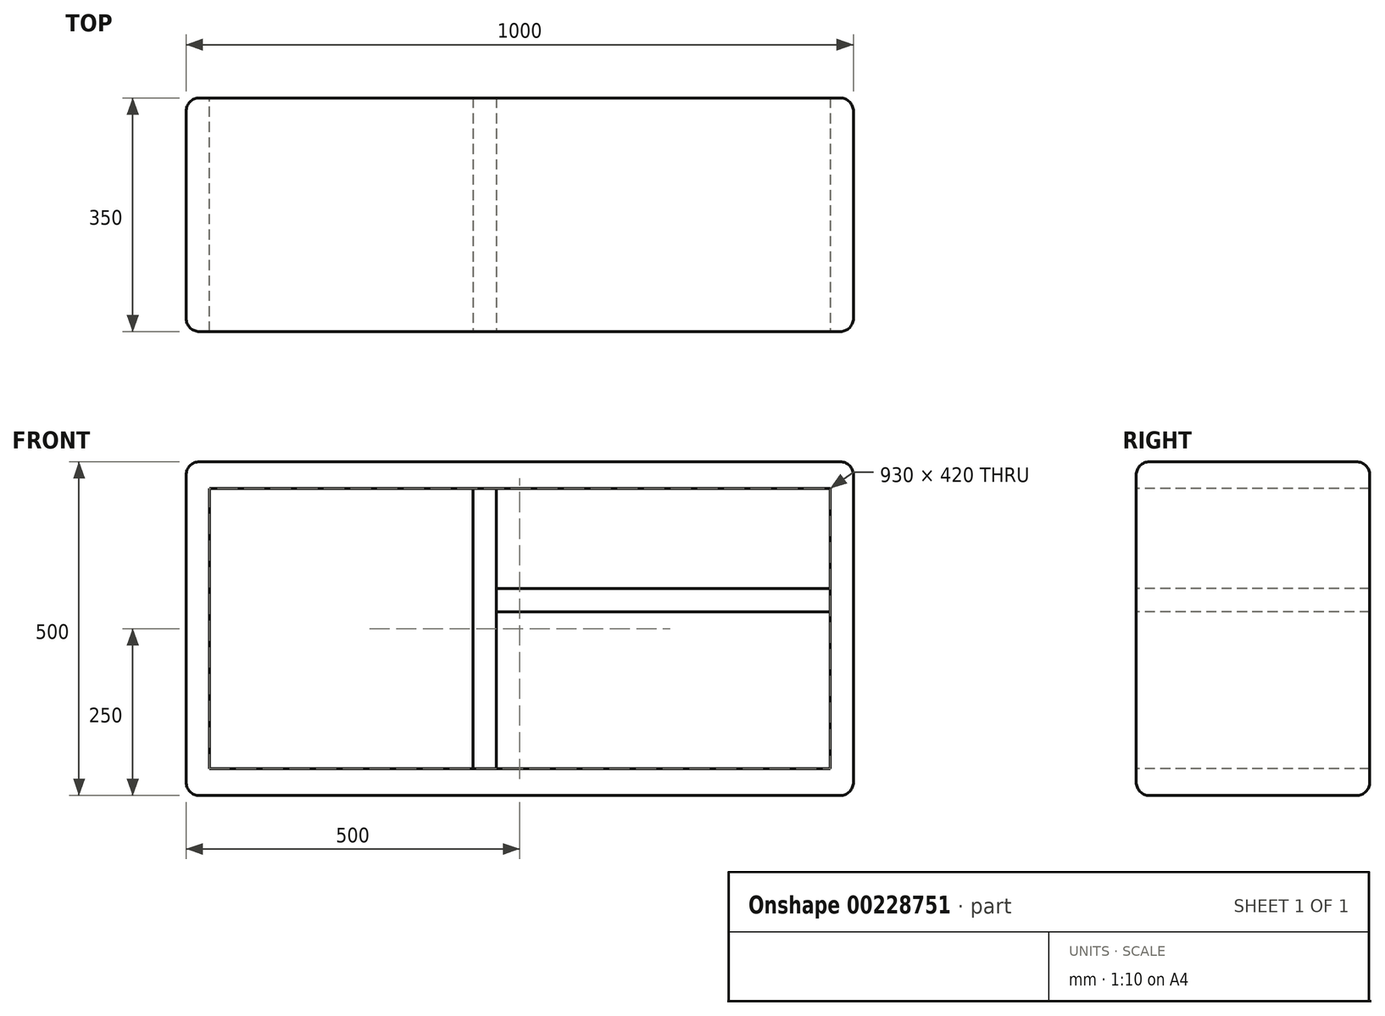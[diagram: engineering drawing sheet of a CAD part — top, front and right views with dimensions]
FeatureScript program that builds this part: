
annotation { "Feature Type Name" : "Feature", "Feature Type Description" : "" }
export const myFeature = defineFeature(function(context is Context, id is Id, definition is map)
    precondition{}
    {
        {
            var Q0;
            Q0=qCreatedBy(makeId("Front.planeOp"),FACE);
            var sketch = newSketch(context, id + "F0", { "sketchPlane" : qUnion([Q0])});
            skLineSegment(sketch, "E0.bottom", {"start": v(500, 250) * mm, "end": v(-500, 250) * mm});
            skLineSegment(sketch, "E0.top", {"start": v(500, -250) * mm, "end": v(-500, -250) * mm});
            skLineSegment(sketch, "E0.left", {"start": v(500, 250) * mm, "end": v(500, -250) * mm});
            skLineSegment(sketch, "E0.right", {"start": v(-500, 250) * mm, "end": v(-500, -250) * mm});
            skPoint(sketch, "E0.middle", {"position": v(0, 0) * mm});
            skLineSegment(sketch, "E1.bottom", {"start": v(465, 210) * mm, "end": v(-465, 210) * mm});
            skLineSegment(sketch, "E1.top", {"start": v(465, -210) * mm, "end": v(-465, -210) * mm});
            skLineSegment(sketch, "E1.left", {"start": v(465, 210) * mm, "end": v(465, -210) * mm});
            skLineSegment(sketch, "E1.right", {"start": v(-465, 210) * mm, "end": v(-465, -210) * mm});
            skSolve(sketch);
        }
        {
            var Q0;
            Q0 = qSketchRegion(id + "F0", true);
            extrude(context, id + "F1", {"entities" : qUnion([Q0]), "depth" : 350 * mm});
        }
        {
            var Q0;
            Q0=makeQuery(id+"F1.opExtrude","CAP_EDGE",EDGE,{"disambiguationData":[OSD([sQuery(id+"F0.wireOp",EDGE,"E0.bottom")])],"isStart":false});
            var Q1;
            Q1=makeQuery(id+"F1.opExtrude","CAP_EDGE",EDGE,{"disambiguationData":[OSD([sQuery(id+"F0.wireOp",EDGE,"E0.left")])],"isStart":false});
            var Q2;
            Q2=makeQuery(id+"F1.opExtrude","CAP_EDGE",EDGE,{"disambiguationData":[OSD([sQuery(id+"F0.wireOp",EDGE,"E0.top")])],"isStart":false});
            var Q3;
            Q3=makeQuery(id+"F1.opExtrude","CAP_EDGE",EDGE,{"disambiguationData":[OSD([sQuery(id+"F0.wireOp",EDGE,"E0.right")])],"isStart":false});
            var Q4;
            Q4=makeQuery(id+"F1.opExtrude","SWEPT_EDGE",EDGE,{"disambiguationData":[OSD([sQuery(id+"F0.wireOp",EDGE,"E0.bottom"),sQuery(id+"F0.wireOp",EDGE,"E0.right")])]});
            var Q5;
            Q5=makeQuery(id+"F1.opExtrude","SWEPT_EDGE",EDGE,{"disambiguationData":[OSD([sQuery(id+"F0.wireOp",EDGE,"E0.bottom"),sQuery(id+"F0.wireOp",EDGE,"E0.left")])]});
            var Q6;
            Q6=makeQuery(id+"F1.opExtrude","SWEPT_EDGE",EDGE,{"disambiguationData":[OSD([sQuery(id+"F0.wireOp",EDGE,"E0.top"),sQuery(id+"F0.wireOp",EDGE,"E0.left")])]});
            var Q7;
            Q7=makeQuery(id+"F1.opExtrude","SWEPT_EDGE",EDGE,{"disambiguationData":[OSD([sQuery(id+"F0.wireOp",EDGE,"E0.top"),sQuery(id+"F0.wireOp",EDGE,"E0.right")])]});
            var Q8;
            Q8=makeQuery(id+"F1.opExtrude","CAP_EDGE",EDGE,{"disambiguationData":[OSD([sQuery(id+"F0.wireOp",EDGE,"E0.right")])],"isStart":true});
            var Q9;
            Q9=makeQuery(id+"F1.opExtrude","CAP_EDGE",EDGE,{"disambiguationData":[OSD([sQuery(id+"F0.wireOp",EDGE,"E0.bottom")])],"isStart":true});
            var Q10;
            Q10=makeQuery(id+"F1.opExtrude","CAP_EDGE",EDGE,{"disambiguationData":[OSD([sQuery(id+"F0.wireOp",EDGE,"E0.left")])],"isStart":true});
            var Q11;
            Q11=makeQuery(id+"F1.opExtrude","CAP_EDGE",EDGE,{"disambiguationData":[OSD([sQuery(id+"F0.wireOp",EDGE,"E0.top")])],"isStart":true});
            fillet(context, id + "F2", {"entities" : qUnion([Q0, Q1, Q2, Q3, Q4, Q5, Q6, Q7, Q8, Q9, Q10, Q11]), "radius" : 20 * mm, "tangentPropagation" : true, "allowEdgeOverflow" : false});
        }
        {
            var Q0;
            Q0=makeQuery(id+"F1.opExtrude","CAP_FACE",FACE,{"disambiguationData":[OSD([sQuery(id+"F0.wireOp",EDGE,"E0.bottom"),sQuery(id+"F0.wireOp",EDGE,"E0.top"),sQuery(id+"F0.wireOp",EDGE,"E0.left"),sQuery(id+"F0.wireOp",EDGE,"E0.right"),sQuery(id+"F0.wireOp",EDGE,"E1.bottom"),sQuery(id+"F0.wireOp",EDGE,"E1.top"),sQuery(id+"F0.wireOp",EDGE,"E1.left"),sQuery(id+"F0.wireOp",EDGE,"E1.right")])],"isStart":false});
            var sketch = newSketch(context, id + "F3", { "sketchPlane" : qUnion([Q0])});
            skLineSegment(sketch, "E2.bottom", {"start": v(-70, 210) * mm, "end": v(-35, 210) * mm});
            skLineSegment(sketch, "E2.top", {"start": v(-70, -210) * mm, "end": v(-35, -210) * mm});
            skLineSegment(sketch, "E2.left", {"start": v(-70, 210) * mm, "end": v(-70, -210) * mm});
            skLineSegment(sketch, "E2.right", {"start": v(-35, 210) * mm, "end": v(-35, -210) * mm});
            skSolve(sketch);
        }
        {
            var Q0;
            Q0 = qSketchRegion(id + "F3", true);
            extrude(context, id + "F4", {"entities" : qUnion([Q0]), "oppositeDirection" : true, "depth" : 350 * mm});
        }
        {
            var Q0;
            Q0=makeQuery(id+"F4.opExtrude","CAP_FACE",FACE,{"disambiguationData":[OSD([sQuery(id+"F3.wireOp",EDGE,"E2.bottom"),sQuery(id+"F3.wireOp",EDGE,"E2.top"),sQuery(id+"F3.wireOp",EDGE,"E2.left"),sQuery(id+"F3.wireOp",EDGE,"E2.right")])],"isStart":true});
            var sketch = newSketch(context, id + "F5", { "sketchPlane" : qUnion([Q0])});
            skLineSegment(sketch, "E3.bottom", {"start": v(-35, 60) * mm, "end": v(465, 60) * mm});
            skLineSegment(sketch, "E3.top", {"start": v(-35, 25) * mm, "end": v(465, 25) * mm});
            skLineSegment(sketch, "E3.left", {"start": v(-35, 60) * mm, "end": v(-35, 25) * mm});
            skLineSegment(sketch, "E3.right", {"start": v(465, 60) * mm, "end": v(465, 25) * mm});
            skSolve(sketch);
        }
        {
            var Q0;
            Q0 = qSketchRegion(id + "F5", true);
            extrude(context, id + "F6", {"entities" : qUnion([Q0]), "oppositeDirection" : true, "depth" : 350 * mm});
        }
    });
